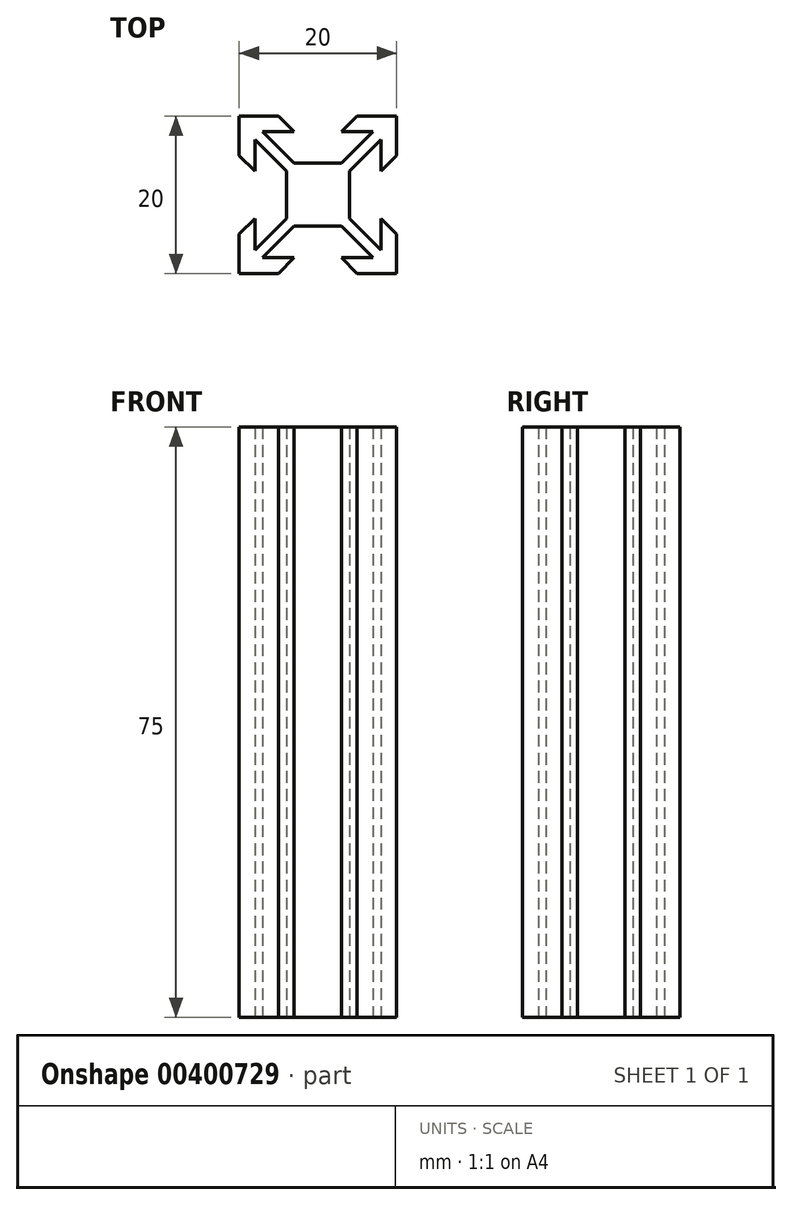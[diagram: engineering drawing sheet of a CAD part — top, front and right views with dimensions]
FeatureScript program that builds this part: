
annotation { "Feature Type Name" : "Feature", "Feature Type Description" : "" }
export const myFeature = defineFeature(function(context is Context, id is Id, definition is map)
    precondition{}
    {
        {
            var Q0;
            Q0=qCreatedBy(makeId("Top.planeOp"),FACE);
            var sketch = newSketch(context, id + "F0", { "sketchPlane" : qUnion([Q0])});
            skLineSegment(sketch, "E0.bottom", {"start": v(10, 10) * mm, "end": v(-10, 10) * mm});
            skLineSegment(sketch, "E0.top", {"start": v(10, -10) * mm, "end": v(-10, -10) * mm});
            skLineSegment(sketch, "E0.left", {"start": v(10, 10) * mm, "end": v(10, -10) * mm});
            skLineSegment(sketch, "E0.right", {"start": v(-10, 10) * mm, "end": v(-10, -10) * mm});
            skPoint(sketch, "E0.middle", {"position": v(0, 0) * mm});
            skLineSegment(sketch, "E1.bottom", {"start": v(4, -4) * mm, "end": v(-4, -4) * mm});
            skLineSegment(sketch, "E1.top", {"start": v(4, 4) * mm, "end": v(-4, 4) * mm});
            skLineSegment(sketch, "E1.left", {"start": v(4, -4) * mm, "end": v(4, 4) * mm});
            skLineSegment(sketch, "E1.right", {"start": v(-4, -4) * mm, "end": v(-4, 4) * mm});
            skLineSegment(sketch, "E2", {"start": v(4, -4) * mm, "end": v(10, -10) * mm});
            skLineSegment(sketch, "E3", {"start": v(10, -10) * mm, "end": v(10, -5) * mm});
            skLineSegment(sketch, "E4", {"start": v(8, -7) * mm, "end": v(4, -3) * mm});
            skLineSegment(sketch, "E5", {"start": v(10, -10) * mm, "end": v(5, -10) * mm});
            skLineSegment(sketch, "E6", {"start": v(7, -8) * mm, "end": v(3, -4) * mm});
            skLineSegment(sketch, "E7", {"start": v(5, -10) * mm, "end": v(3, -8) * mm});
            skLineSegment(sketch, "E8", {"start": v(3, -8) * mm, "end": v(7, -8) * mm});
            skLineSegment(sketch, "E9", {"start": v(10, -5) * mm, "end": v(8, -3) * mm});
            skLineSegment(sketch, "E10", {"start": v(8, -3) * mm, "end": v(8, -7) * mm});
            skLineSegment(sketch, "E11.top", {"start": v(10, 10) * mm, "end": v(10, 5) * mm});
            skLineSegment(sketch, "E11.left", {"start": v(5, 10) * mm, "end": v(10, 10) * mm});
            skLineSegment(sketch, "E12", {"start": v(4, 4) * mm, "end": v(10, 10) * mm});
            skLineSegment(sketch, "E13", {"start": v(10, 10) * mm, "end": v(5, 10) * mm});
            skLineSegment(sketch, "E14", {"start": v(7, 8) * mm, "end": v(3, 4) * mm});
            skLineSegment(sketch, "E15", {"start": v(8, 7) * mm, "end": v(4, 3) * mm});
            skLineSegment(sketch, "E16", {"start": v(10, 5) * mm, "end": v(8, 3) * mm});
            skLineSegment(sketch, "E17", {"start": v(8, 3) * mm, "end": v(8, 7) * mm});
            skLineSegment(sketch, "E18", {"start": v(5, 10) * mm, "end": v(3, 8) * mm});
            skLineSegment(sketch, "E19", {"start": v(3, 8) * mm, "end": v(7, 8) * mm});
            skLineSegment(sketch, "E20.top", {"start": v(-10, -10) * mm, "end": v(-10, -5) * mm});
            skLineSegment(sketch, "E20.left", {"start": v(-5, -10) * mm, "end": v(-10, -10) * mm});
            skLineSegment(sketch, "E21", {"start": v(-4, -4) * mm, "end": v(-10, -10) * mm});
            skLineSegment(sketch, "E22", {"start": v(-10, -10) * mm, "end": v(-5, -10) * mm});
            skLineSegment(sketch, "E23", {"start": v(-7, -8) * mm, "end": v(-3, -4) * mm});
            skLineSegment(sketch, "E24", {"start": v(-8, -7) * mm, "end": v(-4, -3) * mm});
            skLineSegment(sketch, "E25", {"start": v(-10, -5) * mm, "end": v(-8, -3) * mm});
            skLineSegment(sketch, "E26", {"start": v(-8, -3) * mm, "end": v(-8, -7) * mm});
            skLineSegment(sketch, "E27", {"start": v(-5, -10) * mm, "end": v(-3, -8) * mm});
            skLineSegment(sketch, "E28", {"start": v(-3, -8) * mm, "end": v(-7, -8) * mm});
            skLineSegment(sketch, "E29.top", {"start": v(-10, 10) * mm, "end": v(-5, 10) * mm});
            skLineSegment(sketch, "E29.left", {"start": v(-10, 5) * mm, "end": v(-10, 10) * mm});
            skLineSegment(sketch, "E30", {"start": v(-4, 4) * mm, "end": v(-10, 10) * mm});
            skLineSegment(sketch, "E31", {"start": v(-10, 10) * mm, "end": v(-10, 5) * mm});
            skLineSegment(sketch, "E32", {"start": v(-8, 7) * mm, "end": v(-4, 3) * mm});
            skLineSegment(sketch, "E33", {"start": v(-7, 8) * mm, "end": v(-3, 4) * mm});
            skLineSegment(sketch, "E34", {"start": v(-5, 10) * mm, "end": v(-3, 8) * mm});
            skLineSegment(sketch, "E35", {"start": v(-3, 8) * mm, "end": v(-7, 8) * mm});
            skLineSegment(sketch, "E36", {"start": v(-10, 5) * mm, "end": v(-8, 3) * mm});
            skLineSegment(sketch, "E37", {"start": v(-8, 3) * mm, "end": v(-8, 7) * mm});
            skSolve(sketch);
        }
        {
            var Q0;
            {var subQ1=sQuery(id+"F0.wireOp",EDGE,"E1.bottom");var subQ13=makeQuery(id+"F0.imprint","INTERSECT",VERTEX,{"derivedFrom":[subQ1,sQuery(id+"F0.wireOp",EDGE,"E6")]});Q0=makeQuery(id+"F0.imprint","IMPRINT",FACE,{"disambiguationData":[TD([[makeQuery(id+"F0.imprint","IMPRINT",EDGE,{"disambiguationData":[TD([[subQ13,-1.0]])],"derivedFrom":subQ1}),-1.0]])]});}
            var Q1;
            {var subQ0=sQuery(id+"F0.wireOp",EDGE,"E21");Q1=makeQuery(id+"F0.imprint","IMPRINT",FACE,{"disambiguationData":[TD([[makeQuery(id+"F0.imprint","IMPRINT",EDGE,{"derivedFrom":subQ0}),-1.0]])]});}
            var Q2;
            {var subQ0=sQuery(id+"F0.wireOp",EDGE,"E21");Q2=makeQuery(id+"F0.imprint","IMPRINT",FACE,{"disambiguationData":[TD([[makeQuery(id+"F0.imprint","IMPRINT",EDGE,{"derivedFrom":subQ0}),1.0]])]});}
            var Q3;
            {var subQ1=sQuery(id+"F0.wireOp",EDGE,"E2");Q3=makeQuery(id+"F0.imprint","IMPRINT",FACE,{"disambiguationData":[TD([[makeQuery(id+"F0.imprint","IMPRINT",EDGE,{"derivedFrom":subQ1}),-1.0]])]});}
            var Q4;
            {var subQ1=sQuery(id+"F0.wireOp",EDGE,"E2");Q4=makeQuery(id+"F0.imprint","IMPRINT",FACE,{"disambiguationData":[TD([[makeQuery(id+"F0.imprint","IMPRINT",EDGE,{"derivedFrom":subQ1}),1.0]])]});}
            var Q5;
            {var subQ1=sQuery(id+"F0.wireOp",EDGE,"E12");Q5=makeQuery(id+"F0.imprint","IMPRINT",FACE,{"disambiguationData":[TD([[makeQuery(id+"F0.imprint","IMPRINT",EDGE,{"derivedFrom":subQ1}),-1.0]])]});}
            var Q6;
            {var subQ0=sQuery(id+"F0.wireOp",EDGE,"E12");Q6=makeQuery(id+"F0.imprint","IMPRINT",FACE,{"disambiguationData":[TD([[makeQuery(id+"F0.imprint","IMPRINT",EDGE,{"derivedFrom":subQ0}),1.0]])]});}
            var Q7;
            {var subQ1=sQuery(id+"F0.wireOp",EDGE,"E30");Q7=makeQuery(id+"F0.imprint","IMPRINT",FACE,{"disambiguationData":[TD([[makeQuery(id+"F0.imprint","IMPRINT",EDGE,{"derivedFrom":subQ1}),-1.0]])]});}
            var Q8;
            {var subQ0=sQuery(id+"F0.wireOp",EDGE,"E30");Q8=makeQuery(id+"F0.imprint","IMPRINT",FACE,{"disambiguationData":[TD([[makeQuery(id+"F0.imprint","IMPRINT",EDGE,{"derivedFrom":subQ0}),1.0]])]});}
            extrude(context, id + "F1", {"entities" : qUnion([Q0, Q1, Q2, Q3, Q4, Q5, Q6, Q7, Q8]), "depth" : 50 * mm});
        }
        {
            var Q0;
            Q0=makeQuery(id+"F1.opExtrude","CAP_FACE",FACE,{"disambiguationData":[OSD([sQuery(id+"F0.wireOp",EDGE,"E1.bottom"),sQuery(id+"F0.wireOp",EDGE,"E1.top"),sQuery(id+"F0.wireOp",EDGE,"E1.left"),sQuery(id+"F0.wireOp",EDGE,"E1.right"),sQuery(id+"F0.wireOp",EDGE,"E3"),sQuery(id+"F0.wireOp",EDGE,"E4"),sQuery(id+"F0.wireOp",EDGE,"E5"),sQuery(id+"F0.wireOp",EDGE,"E6"),sQuery(id+"F0.wireOp",EDGE,"E7"),sQuery(id+"F0.wireOp",EDGE,"E8"),sQuery(id+"F0.wireOp",EDGE,"E9"),sQuery(id+"F0.wireOp",EDGE,"E10"),sQuery(id+"F0.wireOp",EDGE,"E13"),sQuery(id+"F0.wireOp",EDGE,"E14"),sQuery(id+"F0.wireOp",EDGE,"E11.top"),sQuery(id+"F0.wireOp",EDGE,"E15"),sQuery(id+"F0.wireOp",EDGE,"E16"),sQuery(id+"F0.wireOp",EDGE,"E17"),sQuery(id+"F0.wireOp",EDGE,"E18"),sQuery(id+"F0.wireOp",EDGE,"E19"),sQuery(id+"F0.wireOp",EDGE,"E22"),sQuery(id+"F0.wireOp",EDGE,"E23"),sQuery(id+"F0.wireOp",EDGE,"E20.top"),sQuery(id+"F0.wireOp",EDGE,"E24"),sQuery(id+"F0.wireOp",EDGE,"E25"),sQuery(id+"F0.wireOp",EDGE,"E26"),sQuery(id+"F0.wireOp",EDGE,"E27"),sQuery(id+"F0.wireOp",EDGE,"E28"),sQuery(id+"F0.wireOp",EDGE,"E31"),sQuery(id+"F0.wireOp",EDGE,"E32"),sQuery(id+"F0.wireOp",EDGE,"E29.top"),sQuery(id+"F0.wireOp",EDGE,"E33"),sQuery(id+"F0.wireOp",EDGE,"E34"),sQuery(id+"F0.wireOp",EDGE,"E35"),sQuery(id+"F0.wireOp",EDGE,"E36"),sQuery(id+"F0.wireOp",EDGE,"E37")])],"isStart":false});
            extrude(context, id + "F2", {"entities" : qUnion([Q0]), "operationType" : NewBodyOperationType.ADD, "depth" : 25 * mm, "offsetDistance" : 25 * mm});
        }
    });
